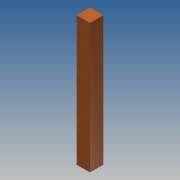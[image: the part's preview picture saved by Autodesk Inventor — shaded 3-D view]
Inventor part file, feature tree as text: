
AUTODESK INVENTOR PART (.ipt)
format: ipt  version: 2013 (Build 170138000, 138)  size: 74,240 bytes
history: native  units: in
note: dims shown in document units (in); Inventor stores cm internally (conversion verified against a paired STEP export)
features: extrude x1, sketch x1
ambient origin geometry x8: Origin, YZ Plane, XZ Plane, XY Plane, X Axis, Y Axis, Z Axis, Center Point
bodies: Solid1 (feature_tree)
feature tree (2):
  extrude  "Extrusion1"  Depth=3.5in
  sketch  "Sketch1"  dims[d0=3.5in d1=3.5in d2=34.0in d3=0.0in]
